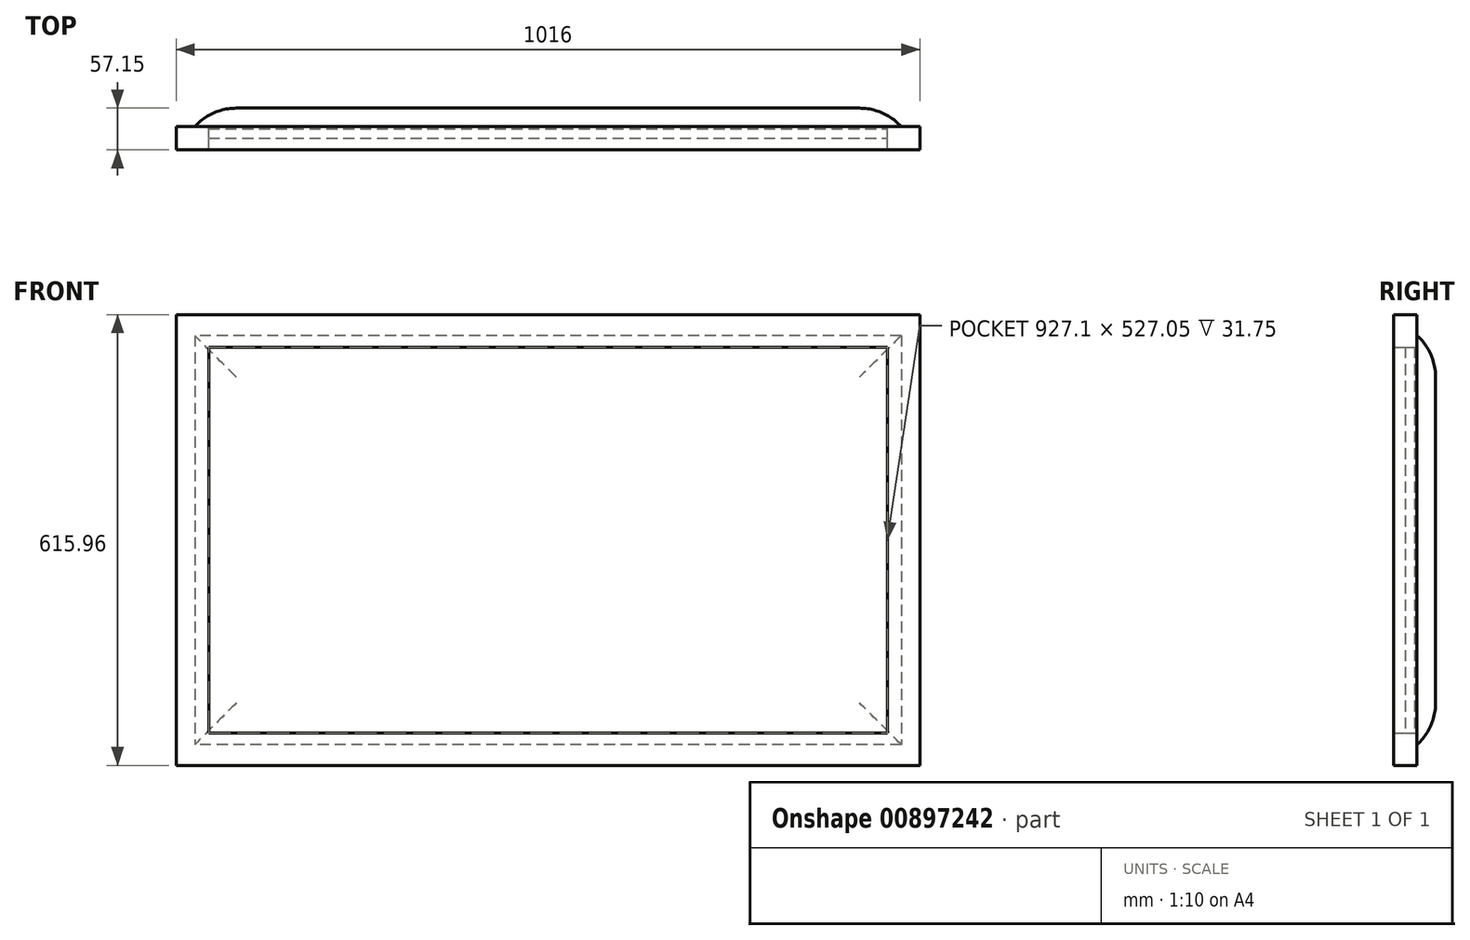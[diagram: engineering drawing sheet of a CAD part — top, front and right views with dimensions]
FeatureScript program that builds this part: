
annotation { "Feature Type Name" : "Feature", "Feature Type Description" : "" }
export const myFeature = defineFeature(function(context is Context, id is Id, definition is map)
    precondition{}
    {
        {
            var Q0;
            Q0=qCreatedBy(makeId("Front.planeOp"),FACE);
            var sketch = newSketch(context, id + "F0", { "sketchPlane" : qUnion([Q0])});
            skLineSegment(sketch, "E0.bottom", {"start": v(-463.55, 263.52) * mm, "end": v(463.55, 263.52) * mm});
            skLineSegment(sketch, "E0.top", {"start": v(-463.55, -263.52) * mm, "end": v(463.55, -263.52) * mm});
            skLineSegment(sketch, "E0.left", {"start": v(-463.55, 263.52) * mm, "end": v(-463.55, -263.52) * mm});
            skLineSegment(sketch, "E0.right", {"start": v(463.55, 263.52) * mm, "end": v(463.55, -263.52) * mm});
            skPoint(sketch, "E0.middle", {"position": v(0, 0) * mm});
            skSolve(sketch);
        }
        {
            var Q0;
            Q0=makeQuery(id+"F0.imprint","IMPRINT",FACE,{"disambiguationData":[TD([[makeQuery(id+"F0.imprint","IMPRINT",EDGE,{"derivedFrom":sQuery(id+"F0.wireOp",EDGE,"E0.bottom")}),-1.0]])]});
            extrude(context, id + "F1", {"entities" : qUnion([Q0]), "depth" : 12.7 * mm, "offsetDistance" : 25.4 * mm});
        }
        {
            var Q0;
            Q0=makeQuery(id+"F1.opExtrude","CAP_FACE",FACE,{"disambiguationData":[OSD([sQuery(id+"F0.wireOp",EDGE,"E0.bottom"),sQuery(id+"F0.wireOp",EDGE,"E0.top"),sQuery(id+"F0.wireOp",EDGE,"E0.left"),sQuery(id+"F0.wireOp",EDGE,"E0.right")])],"isStart":false});
            var sketch = newSketch(context, id + "F2", { "sketchPlane" : qUnion([Q0])});
            skLineSegment(sketch, "E1.0", {"start": v(-508, 307.97) * mm, "end": v(-508, -307.97) * mm});
            skLineSegment(sketch, "E1.1", {"start": v(-508, 307.97) * mm, "end": v(508, 307.97) * mm});
            skLineSegment(sketch, "E1.2", {"start": v(508, 307.97) * mm, "end": v(508, -307.97) * mm});
            skLineSegment(sketch, "E1.3", {"start": v(-508, -307.97) * mm, "end": v(508, -307.97) * mm});
            skLineSegment(sketch, "E2.0", {"start": v(-463.55, 263.52) * mm, "end": v(-463.55, -263.52) * mm});
            skLineSegment(sketch, "E3.0", {"start": v(-463.55, 263.52) * mm, "end": v(463.55, 263.52) * mm});
            skLineSegment(sketch, "E4.0", {"start": v(-463.55, -263.52) * mm, "end": v(463.55, -263.52) * mm});
            skLineSegment(sketch, "E5.0", {"start": v(463.55, 263.52) * mm, "end": v(463.55, -263.52) * mm});
            skSolve(sketch);
        }
        {
            var Q0;
            Q0 = qSketchRegion(id + "F2", true);
            extrude(context, id + "F3", {"entities" : qUnion([Q0]), "endBound" : BoundingType.SYMMETRIC, "depth" : 31.75 * mm, "offsetDistance" : 25.4 * mm});
        }
        {
            var Q0;
            Q0=makeQuery(id+"F3.opExtrude","CAP_FACE",FACE,{"disambiguationData":[OSD([sQuery(id+"F2.wireOp",EDGE,"E1.0"),sQuery(id+"F2.wireOp",EDGE,"E1.1"),sQuery(id+"F2.wireOp",EDGE,"E1.2"),sQuery(id+"F2.wireOp",EDGE,"E1.3"),sQuery(id+"F2.wireOp",EDGE,"E2.0"),sQuery(id+"F2.wireOp",EDGE,"E3.0"),sQuery(id+"F2.wireOp",EDGE,"E4.0"),sQuery(id+"F2.wireOp",EDGE,"E5.0")])],"isStart":true});
            var sketch = newSketch(context, id + "F4", { "sketchPlane" : qUnion([Q0])});
            skLineSegment(sketch, "E6.bottom", {"start": v(-482.6, 279.4) * mm, "end": v(482.6, 279.4) * mm});
            skLineSegment(sketch, "E6.top", {"start": v(-482.6, -279.4) * mm, "end": v(482.6, -279.4) * mm});
            skLineSegment(sketch, "E6.left", {"start": v(-482.6, 279.4) * mm, "end": v(-482.6, -279.4) * mm});
            skLineSegment(sketch, "E6.right", {"start": v(482.6, 279.4) * mm, "end": v(482.6, -279.4) * mm});
            skPoint(sketch, "E6.middle", {"position": v(0, 0) * mm});
            skSolve(sketch);
        }
        {
            var Q0;
            Q0 = qSketchRegion(id + "F4", true);
            extrude(context, id + "F5", {"entities" : qUnion([Q0]), "operationType" : NewBodyOperationType.ADD, "depth" : 25.4 * mm, "offsetDistance" : 25.4 * mm});
        }
        {
            var Q0;
            Q0=makeQuery(id+"F5.opExtrude","CAP_EDGE",EDGE,{"disambiguationData":[OSD([sQuery(id+"F4.wireOp",EDGE,"E6.left")])],"isStart":false});
            var Q1;
            Q1=makeQuery(id+"F5.opExtrude","CAP_EDGE",EDGE,{"disambiguationData":[OSD([sQuery(id+"F4.wireOp",EDGE,"E6.bottom")])],"isStart":false});
            var Q2;
            Q2=makeQuery(id+"F5.opExtrude","CAP_EDGE",EDGE,{"disambiguationData":[OSD([sQuery(id+"F4.wireOp",EDGE,"E6.right")])],"isStart":false});
            var Q3;
            Q3=makeQuery(id+"F5.opExtrude","CAP_EDGE",EDGE,{"disambiguationData":[OSD([sQuery(id+"F4.wireOp",EDGE,"E6.top")])],"isStart":false});
            fillet(context, id + "F6", {"entities" : qUnion([Q0, Q1, Q2, Q3]), "radius" : 76.2 * mm, "tangentPropagation" : true, "allowEdgeOverflow" : false});
        }
    });
